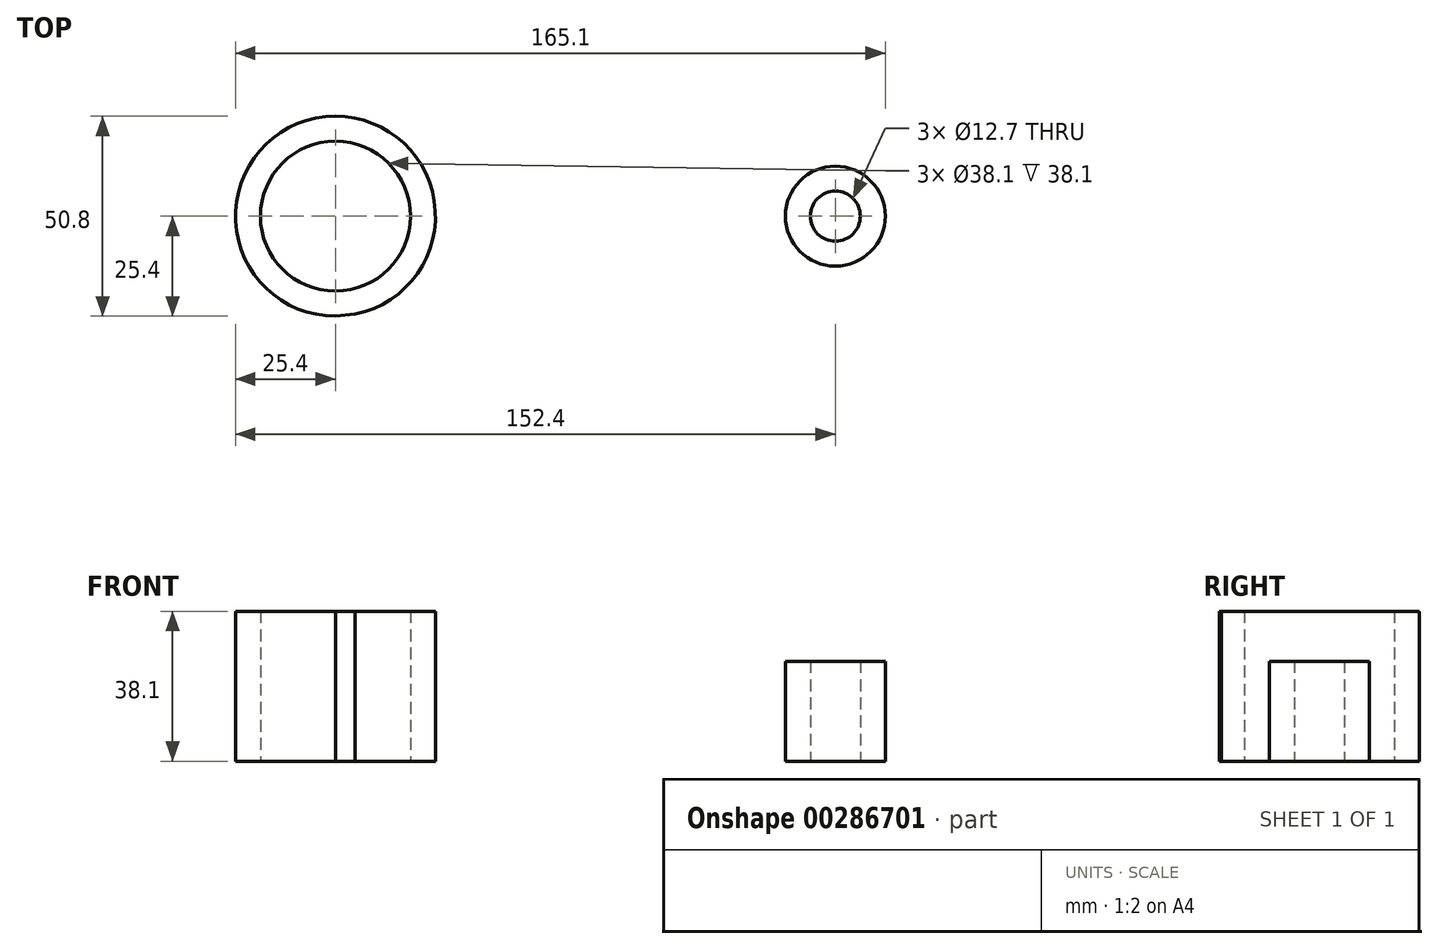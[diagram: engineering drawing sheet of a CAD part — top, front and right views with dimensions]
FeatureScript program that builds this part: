
annotation { "Feature Type Name" : "Feature", "Feature Type Description" : "" }
export const myFeature = defineFeature(function(context is Context, id is Id, definition is map)
    precondition{}
    {
        {
            var Q0;
            Q0=qCreatedBy(makeId("Top.planeOp"),FACE);
            var sketch = newSketch(context, id + "F0", { "sketchPlane" : qUnion([Q0])});
            skArc(sketch, "E0", {"start": v(5.03, -24.9) * mm, "mid": v(-2.53, 25.27) * mm, "end": v(0, -25.4) * mm});
            skCircle(sketch, "E1", {"center": v(0, 0) * mm, "radius": 19.05 * mm});
            skCircle(sketch, "E2", {"center": v(127, 0) * mm, "radius": 12.7 * mm});
            skCircle(sketch, "E3", {"center": v(127, 0) * mm, "radius": 6.35 * mm});
            skLineSegment(sketch, "E4", {"start": v(0, -25.4) * mm, "end": v(5.03, -24.9) * mm});
            skArc(sketch, "E5", {"start": v(38.1, 6.35) * mm, "mid": v(31.75, 0) * mm, "end": v(38.1, -6.35) * mm});
            skArc(sketch, "E6", {"start": v(88.9, -6.35) * mm, "mid": v(95.25, 0) * mm, "end": v(88.9, 6.35) * mm});
            skLineSegment(sketch, "E7", {"start": v(38.1, 6.35) * mm, "end": v(88.9, 6.35) * mm});
            skLineSegment(sketch, "E8", {"start": v(38.1, -6.35) * mm, "end": v(88.9, -6.35) * mm});
            skPoint(sketch, "E9.orphan", {"position": v(127, 12.7) * mm});
            skPoint(sketch, "E10.orphan", {"position": v(0, 12.7) * mm});
            skPoint(sketch, "E11.orphan", {"position": v(127, -12.7) * mm});
            skLineSegment(sketch, "E12", {"start": v(0, 25.53) * mm, "end": v(128.27, 12.64) * mm});
            skLineSegment(sketch, "E13", {"start": v(0, -25.53) * mm, "end": v(128.27, -12.64) * mm});
            skSolve(sketch);
        }
        {
            var Q0;
            Q0=makeQuery(id+"F0.imprint","IMPRINT",FACE,{"disambiguationData":[TD([[makeQuery(id+"F0.imprint","IMPRINT",EDGE,{"derivedFrom":sQuery(id+"F0.wireOp",EDGE,"E1")}),-1.0]])]});
            extrude(context, id + "F1", {"entities" : qUnion([Q0]), "depth" : 38.1 * mm});
        }
        {
            var Q0;
            Q0=makeQuery(id+"F0.imprint","IMPRINT",FACE,{"disambiguationData":[TD([[makeQuery(id+"F0.imprint","IMPRINT",EDGE,{"derivedFrom":sQuery(id+"F0.wireOp",EDGE,"E3")}),-1.0]])]});
            extrude(context, id + "F2", {"entities" : qUnion([Q0]), "depth" : 25.4 * mm});
        }
    });
